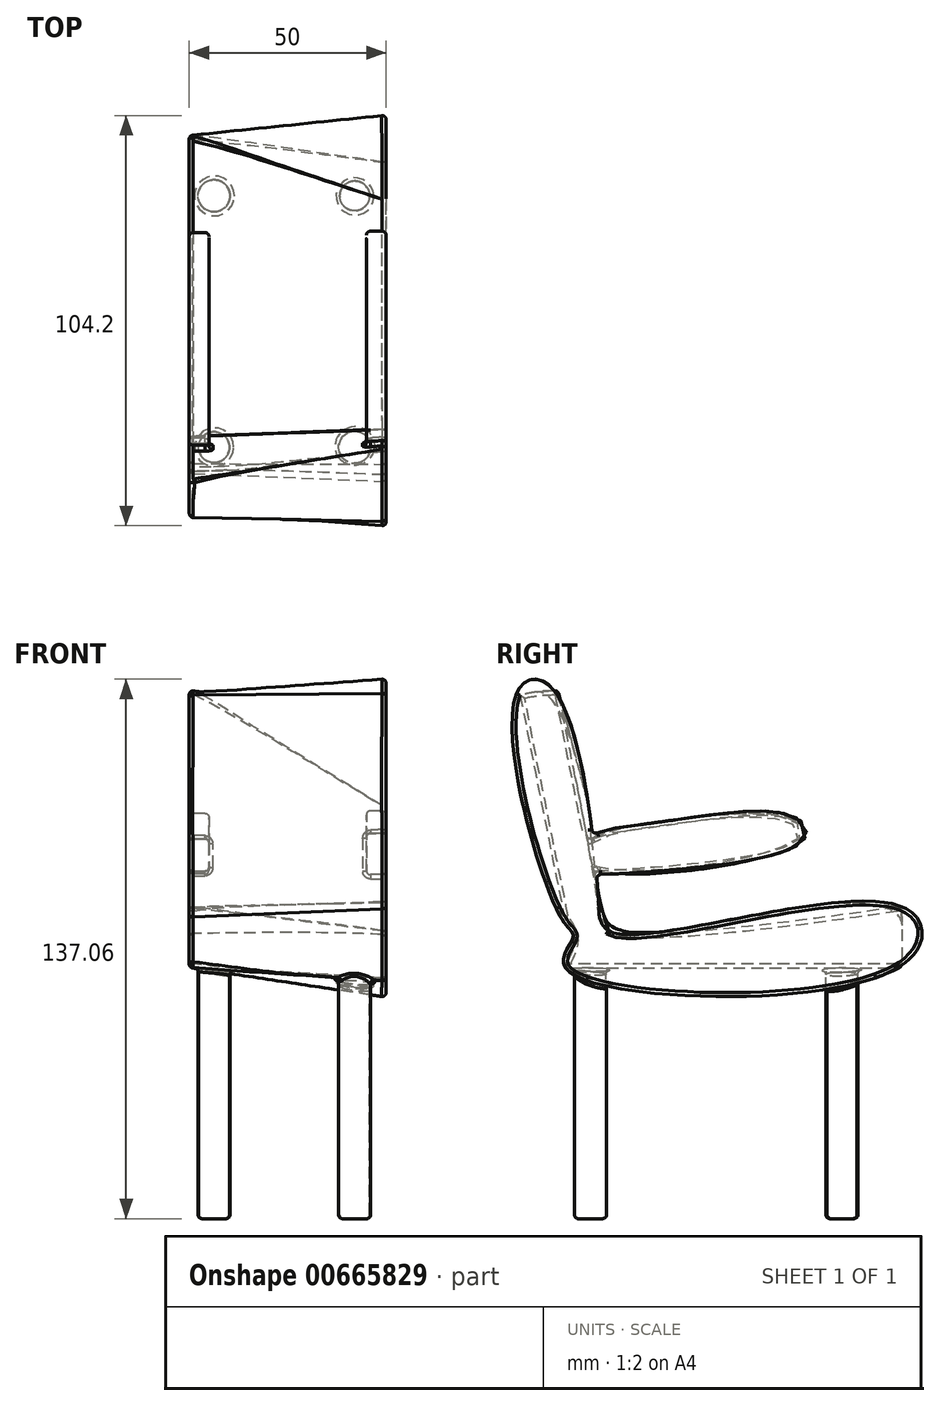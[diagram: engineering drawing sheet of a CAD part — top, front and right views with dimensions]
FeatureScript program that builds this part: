
annotation { "Feature Type Name" : "Feature", "Feature Type Description" : "" }
export const myFeature = defineFeature(function(context is Context, id is Id, definition is map)
    precondition{}
    {
        {
            var Q0;
            Q0=qCreatedBy(makeId("Right.planeOp"),FACE);
            var sketch = newSketch(context, id + "F0", { "sketchPlane" : qUnion([Q0])});
            skLineSegment(sketch, "E0", {"start": v(-50.58, 53.8) * mm, "end": v(-39.33, -2.57) * mm});
            skLineSegment(sketch, "E1", {"start": v(-50.58, 53.8) * mm, "end": v(-41.14, 55.7) * mm});
            skLineSegment(sketch, "E2", {"start": v(-41.14, 55.7) * mm, "end": v(-30.03, 0) * mm});
            skFitSpline(sketch, "E3", {"points": [v(-30.03, 0) * mm, v(-30.03, -2.54) * mm, v(-24.88, -6.35) * mm, v(46.15, 0) * mm, v(46.46, 0) * mm], "startDerivative": vector(-1.64, -20.18) * mm, "endDerivative": vector(2.27, -0.83) * mm});
            skLineSegment(sketch, "E4", {"start": v(46.46, 0) * mm, "end": v(46.46, -15.37) * mm});
            skLineSegment(sketch, "E5", {"start": v(46.46, -15.37) * mm, "end": v(-39.66, -15.37) * mm});
            skFitSpline(sketch, "E6", {"points": [v(-39.66, -15.37) * mm, v(-36.82, -8.62) * mm, v(-39.33, -2.57) * mm], "startDerivative": vector(8.26, 13.3) * mm, "endDerivative": vector(-7.75, 12.28) * mm});
            skSolve(sketch);
        }
        {
            var Q0;
            Q0=qCreatedBy(makeId("Right.planeOp"),FACE);
            cPlane(context, id + "F1", {"entities" : qUnion([Q0]), "cplaneType" : CPlaneType.OFFSET, "offset" : 50 * mm, "width" : 150 * mm, "height" : 150 * mm});
        }
        {
            var Q0;
            Q0=qCreatedBy(id+"F1.planeOp",FACE);
            var sketch = newSketch(context, id + "F2", { "sketchPlane" : qUnion([Q0])});
            skFitSpline(sketch, "E7", {"points": [v(-51.65, 54.06) * mm, v(-42.1, 55.21) * mm, v(-30.57, 0) * mm, v(-30.31, -3.29) * mm, v(-25.5, -6.94) * mm, v(46.72, 0) * mm, v(46.01, -15.02) * mm, v(-39.1, -15.52) * mm, v(-37.17, -7.84) * mm, v(-39.86, -3.35) * mm, v(-51.65, 54.06) * mm]});
            skSolve(sketch);
        }
        {
            var Q0;
            Q0=makeQuery(id+"F0.imprint","IMPRINT",FACE,{"disambiguationData":[TD([[makeQuery(id+"F0.imprint","IMPRINT",EDGE,{"derivedFrom":sQuery(id+"F0.wireOp",EDGE,"E0")}),1.0]])]});
            var Q1;
            Q1=makeQuery(id+"F2.imprint","IMPRINT",FACE,{"disambiguationData":[TD([[makeQuery(id+"F2.imprint","IMPRINT",EDGE,{"derivedFrom":sQuery(id+"F2.wireOp",EDGE,"E7")}),-1.0]])]});
            loft(context, id + "F3", {"sheetProfilesArray" : [{ "sheetProfileEntities" : qUnion([Q0]) }, { "sheetProfileEntities" : qUnion([Q1]) }]});
        }
        {
            var Q0;
            Q0=qCreatedBy(makeId("Top.planeOp"),FACE);
            cPlane(context, id + "F4", {"entities" : qUnion([Q0]), "cplaneType" : CPlaneType.OFFSET, "offset" : 9.2 * mm, "oppositeDirection" : true, "width" : 150 * mm, "height" : 150 * mm});
        }
        {
            var Q0;
            Q0=qCreatedBy(id+"F4.planeOp",FACE);
            var sketch = newSketch(context, id + "F5", { "sketchPlane" : qUnion([Q0])});
            skCircle(sketch, "E8", {"center": v(6.29, -32.74) * mm, "radius": 3.94 * mm});
            skCircle(sketch, "E9", {"center": v(6.29, 31.14) * mm, "radius": 4.07 * mm});
            skCircle(sketch, "E10", {"center": v(42.02, 31.14) * mm, "radius": 3.8 * mm});
            skCircle(sketch, "E11", {"center": v(42.02, -32.74) * mm, "radius": 4.07 * mm});
            skSolve(sketch);
        }
        {
            var Q0;
            Q0 = qSketchRegion(id + "F5", true);
            extrude(context, id + "F6", {"entities" : qUnion([Q0]), "operationType" : NewBodyOperationType.ADD, "oppositeDirection" : true, "depth" : 70 * mm, "offsetDistance" : 25 * mm});
        }
        {
            var Q0;
            Q0=qCreatedBy(makeId("Right.planeOp"),FACE);
            var sketch = newSketch(context, id + "F7", { "sketchPlane" : qUnion([Q0])});
            skFitSpline(sketch, "E12", {"points": [v(-34.3, 15.81) * mm, v(-12.93, 21.89) * mm, v(18.5, 22.22) * mm, v(20.95, 16.94) * mm, v(-33.45, 10) * mm, v(-34.3, 15.81) * mm]});
            skSolve(sketch);
        }
        {
            var Q0;
            Q0 = qSketchRegion(id + "F7", true);
            extrude(context, id + "F8", {"entities" : qUnion([Q0]), "operationType" : NewBodyOperationType.ADD, "depth" : 5 * mm, "offsetDistance" : 25 * mm});
        }
        {
            var Q0;
            Q0=qCreatedBy(id+"F1.planeOp",FACE);
            var sketch = newSketch(context, id + "F9", { "sketchPlane" : qUnion([Q0])});
            skFitSpline(sketch, "E13", {"points": [v(-34.26, 16.55) * mm, v(-18.96, 21) * mm, v(14.18, 24.2) * mm, v(21.83, 20.37) * mm, v(19.28, 15.27) * mm, v(-29.16, 8.26) * mm, v(-34.9, 9.53) * mm, v(-34.26, 16.55) * mm]});
            skSolve(sketch);
        }
        {
            var Q0;
            Q0 = qSketchRegion(id + "F9", true);
            extrude(context, id + "F10", {"entities" : qUnion([Q0]), "operationType" : NewBodyOperationType.ADD, "oppositeDirection" : true, "depth" : 5 * mm, "offsetDistance" : 25 * mm});
        }
        {
            var Q0;
            Q0=makeQuery(id+"F3.opLoft","SWEPT_FACE",FACE,{"disambiguationData":[OSD([sQuery(id+"F0.wireOp",EDGE,"E2"),sQuery(id+"F0.wireOp",EDGE,"E3"),sQuery(id+"F0.wireOp",EDGE,"E4"),sQuery(id+"F0.wireOp",EDGE,"E5"),sQuery(id+"F2.wireOp",EDGE,"E7")])]});
            var Q1;
            Q1=makeQuery(id+"F10.boolean.opBoolean","MERGE",FACE,{"derivedFrom":[makeQuery(id+"F3.opLoft","CAP_FACE",FACE,{"disambiguationData":[OSD([makeQuery(id+"F2.imprint","IMPRINT",FACE,{"disambiguationData":[TD([[makeQuery(id+"F2.imprint","IMPRINT",EDGE,{"derivedFrom":sQuery(id+"F2.wireOp",EDGE,"E7")}),-1.0]])]})])],"isStart":true}),makeQuery(id+"F10.opExtrude","CAP_FACE",FACE,{"disambiguationData":[OSD([sQuery(id+"F9.wireOp",EDGE,"E13")])],"isStart":true})]});
            var Q2;
            Q2=makeQuery(id+"F3.opLoft","SWEPT_FACE",FACE,{"disambiguationData":[OSD([sQuery(id+"F0.wireOp",EDGE,"E0"),sQuery(id+"F0.wireOp",EDGE,"E1"),sQuery(id+"F0.wireOp",EDGE,"E2"),sQuery(id+"F0.wireOp",EDGE,"E3"),sQuery(id+"F2.wireOp",EDGE,"E7")])]});
            var Q3;
            Q3=makeQuery(id+"F3.opLoft","SWEPT_FACE",FACE,{"disambiguationData":[OSD([sQuery(id+"F0.wireOp",EDGE,"E1"),sQuery(id+"F0.wireOp",EDGE,"E2"),sQuery(id+"F0.wireOp",EDGE,"E3"),sQuery(id+"F0.wireOp",EDGE,"E4"),sQuery(id+"F2.wireOp",EDGE,"E7")])]});
            var Q4;
            Q4=makeQuery(id+"F8.opExtrude","CAP_EDGE",EDGE,{"disambiguationData":[OSD([sQuery(id+"F7.wireOp",EDGE,"E12")])],"isStart":false});
            var Q5;
            Q5=makeQuery(id+"F8.opExtrude","CAP_EDGE",EDGE,{"disambiguationData":[OSD([sQuery(id+"F7.wireOp",EDGE,"E12")])],"isStart":true});
            var Q6;
            Q6=makeQuery(id+"F8.boolean.opBoolean","MERGE",FACE,{"derivedFrom":[makeQuery(id+"F3.opLoft","CAP_FACE",FACE,{"disambiguationData":[OSD([makeQuery(id+"F0.imprint","IMPRINT",FACE,{"disambiguationData":[TD([[makeQuery(id+"F0.imprint","IMPRINT",EDGE,{"derivedFrom":sQuery(id+"F0.wireOp",EDGE,"E0")}),1.0]])]})])],"isStart":true}),makeQuery(id+"F8.opExtrude","CAP_FACE",FACE,{"disambiguationData":[OSD([sQuery(id+"F7.wireOp",EDGE,"E12")])],"isStart":true})]});
            var Q7;
            Q7=makeQuery(id+"F3.opLoft","SWEPT_FACE",FACE,{"disambiguationData":[OSD([sQuery(id+"F0.wireOp",EDGE,"E0"),sQuery(id+"F0.wireOp",EDGE,"E4"),sQuery(id+"F0.wireOp",EDGE,"E5"),sQuery(id+"F0.wireOp",EDGE,"E6"),sQuery(id+"F2.wireOp",EDGE,"E7")])]});
            var Q8;
            Q8=makeQuery(id+"F6.opExtrude","SWEPT_FACE",FACE,{"disambiguationData":[OSD([sQuery(id+"F5.wireOp",EDGE,"E11")])]});
            var Q9;
            Q9=makeQuery(id+"F6.opExtrude","SWEPT_FACE",FACE,{"disambiguationData":[OSD([sQuery(id+"F5.wireOp",EDGE,"E8")])]});
            var Q10;
            Q10=makeQuery(id+"F6.opExtrude","SWEPT_FACE",FACE,{"disambiguationData":[OSD([sQuery(id+"F5.wireOp",EDGE,"E10")])]});
            var Q11;
            Q11=makeQuery(id+"F6.opExtrude","SWEPT_FACE",FACE,{"disambiguationData":[OSD([sQuery(id+"F5.wireOp",EDGE,"E9")])]});
            var Q12;
            Q12=makeQuery(id+"F10.opExtrude","CAP_EDGE",EDGE,{"disambiguationData":[OSD([sQuery(id+"F9.wireOp",EDGE,"E13")])],"isStart":false});
            fillet(context, id + "F11", {"entities" : qUnion([Q0, Q1, Q2, Q3, Q4, Q5, Q6, Q7, Q8, Q9, Q10, Q11, Q12]), "radius" : 1 * mm, "tangentPropagation" : true, "allowEdgeOverflow" : false});
        }
    });
